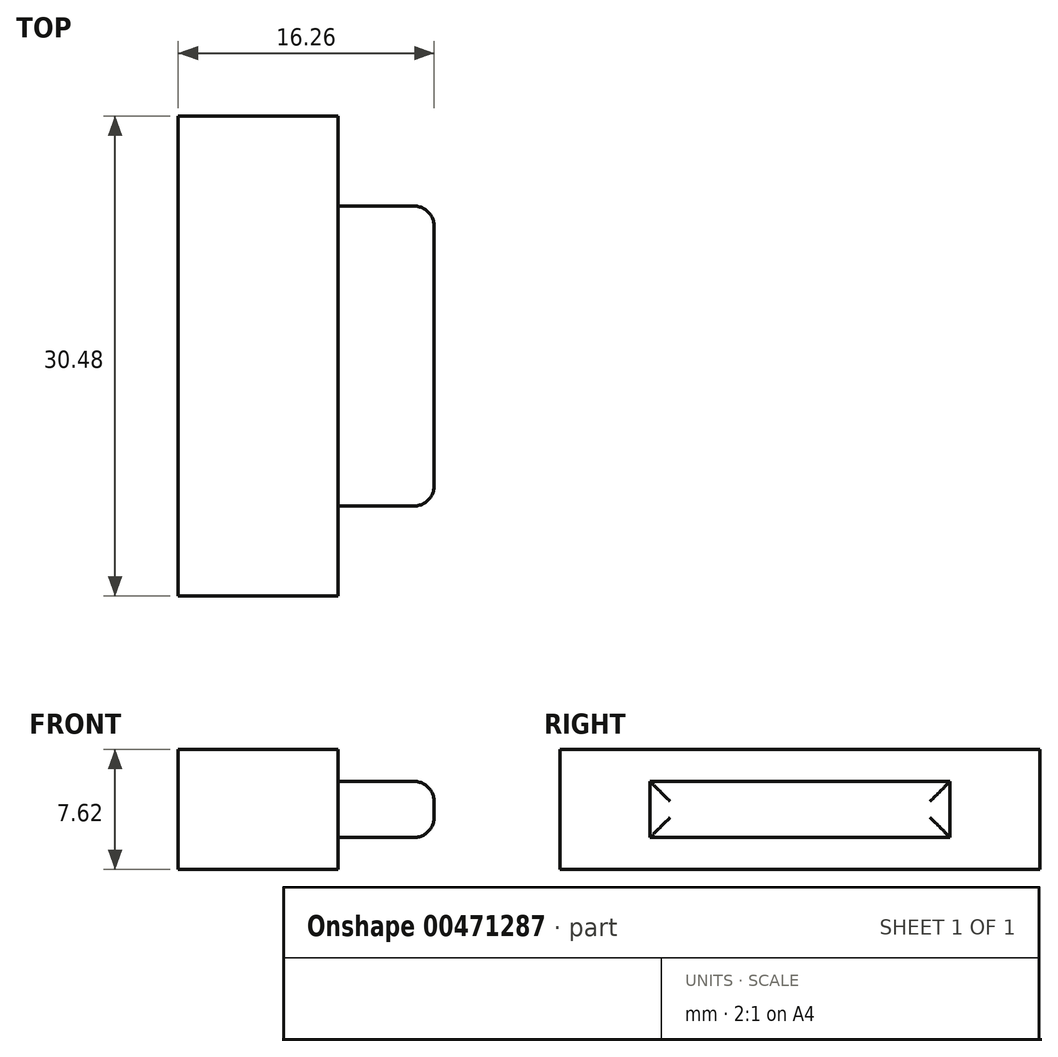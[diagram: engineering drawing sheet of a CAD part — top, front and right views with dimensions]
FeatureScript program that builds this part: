
annotation { "Feature Type Name" : "Feature", "Feature Type Description" : "" }
export const myFeature = defineFeature(function(context is Context, id is Id, definition is map)
    precondition{}
    {
        {
            var Q0;
            Q0=qCreatedBy(makeId("Right.planeOp"),FACE);
            var sketch = newSketch(context, id + "F0", { "sketchPlane" : qUnion([Q0])});
            skLineSegment(sketch, "E0.bottom", {"start": v(-15.24, 3.81) * mm, "end": v(15.24, 3.81) * mm});
            skLineSegment(sketch, "E0.top", {"start": v(-15.24, -3.8) * mm, "end": v(15.24, -3.8) * mm});
            skLineSegment(sketch, "E0.left", {"start": v(-15.24, 3.81) * mm, "end": v(-15.24, -3.8) * mm});
            skLineSegment(sketch, "E0.right", {"start": v(15.24, 3.81) * mm, "end": v(15.24, -3.8) * mm});
            skLineSegment(sketch, "E1.bottom", {"start": v(-9.53, 1.78) * mm, "end": v(9.53, 1.78) * mm});
            skLineSegment(sketch, "E1.top", {"start": v(-9.53, -1.78) * mm, "end": v(9.53, -1.78) * mm});
            skLineSegment(sketch, "E1.left", {"start": v(-9.53, 1.78) * mm, "end": v(-9.53, -1.78) * mm});
            skLineSegment(sketch, "E1.right", {"start": v(9.53, 1.78) * mm, "end": v(9.53, -1.78) * mm});
            skSolve(sketch);
        }
        {
            var Q0;
            Q0=makeQuery(id+"F0.imprint","IMPRINT",FACE,{"disambiguationData":[TD([[makeQuery(id+"F0.imprint","IMPRINT",EDGE,{"derivedFrom":sQuery(id+"F0.wireOp",EDGE,"E0.bottom")}),-1.0]])]});
            var Q1;
            Q1=makeQuery(id+"F0.imprint","IMPRINT",FACE,{"disambiguationData":[TD([[makeQuery(id+"F0.imprint","IMPRINT",EDGE,{"derivedFrom":sQuery(id+"F0.wireOp",EDGE,"E1.bottom")}),-1.0]])]});
            extrude(context, id + "F1", {"entities" : qUnion([Q0, Q1]), "oppositeDirection" : true, "depth" : 10.16 * mm, "offsetDistance" : 25.4 * mm});
        }
        {
            var Q0;
            Q0=makeQuery(id+"F1.opExtrude","CAP_FACE",FACE,{"disambiguationData":[OSD([sQuery(id+"F0.wireOp",EDGE,"E0.bottom"),sQuery(id+"F0.wireOp",EDGE,"E0.top"),sQuery(id+"F0.wireOp",EDGE,"E0.left"),sQuery(id+"F0.wireOp",EDGE,"E0.right")])],"isStart":true});
            var sketch = newSketch(context, id + "F2", { "sketchPlane" : qUnion([Q0])});
            skLineSegment(sketch, "E2.bottom", {"start": v(-9.52, 1.78) * mm, "end": v(9.53, 1.78) * mm});
            skLineSegment(sketch, "E2.top", {"start": v(-9.52, -1.78) * mm, "end": v(9.53, -1.78) * mm});
            skLineSegment(sketch, "E2.left", {"start": v(-9.52, 1.78) * mm, "end": v(-9.52, -1.78) * mm});
            skLineSegment(sketch, "E2.right", {"start": v(9.53, 1.78) * mm, "end": v(9.53, -1.78) * mm});
            skSolve(sketch);
        }
        {
            var Q0;
            Q0 = qSketchRegion(id + "F2", true);
            extrude(context, id + "F3", {"entities" : qUnion([Q0]), "operationType" : NewBodyOperationType.ADD, "depth" : 6.1 * mm, "offsetDistance" : 25.4 * mm});
        }
        {
            var Q0;
            Q0=makeQuery(id+"F3.opExtrude","CAP_EDGE",EDGE,{"disambiguationData":[OSD([sQuery(id+"F2.wireOp",EDGE,"E2.bottom")])],"isStart":false});
            var Q1;
            Q1=makeQuery(id+"F3.opExtrude","CAP_EDGE",EDGE,{"disambiguationData":[OSD([sQuery(id+"F2.wireOp",EDGE,"E2.left")])],"isStart":false});
            var Q2;
            Q2=makeQuery(id+"F3.opExtrude","CAP_EDGE",EDGE,{"disambiguationData":[OSD([sQuery(id+"F2.wireOp",EDGE,"E2.top")])],"isStart":false});
            var Q3;
            Q3=makeQuery(id+"F3.opExtrude","CAP_EDGE",EDGE,{"disambiguationData":[OSD([sQuery(id+"F2.wireOp",EDGE,"E2.right")])],"isStart":false});
            fillet(context, id + "F4", {"entities" : qUnion([Q0, Q1, Q2, Q3]), "radius" : 1.27 * mm, "tangentPropagation" : true, "allowEdgeOverflow" : false});
        }
    });
